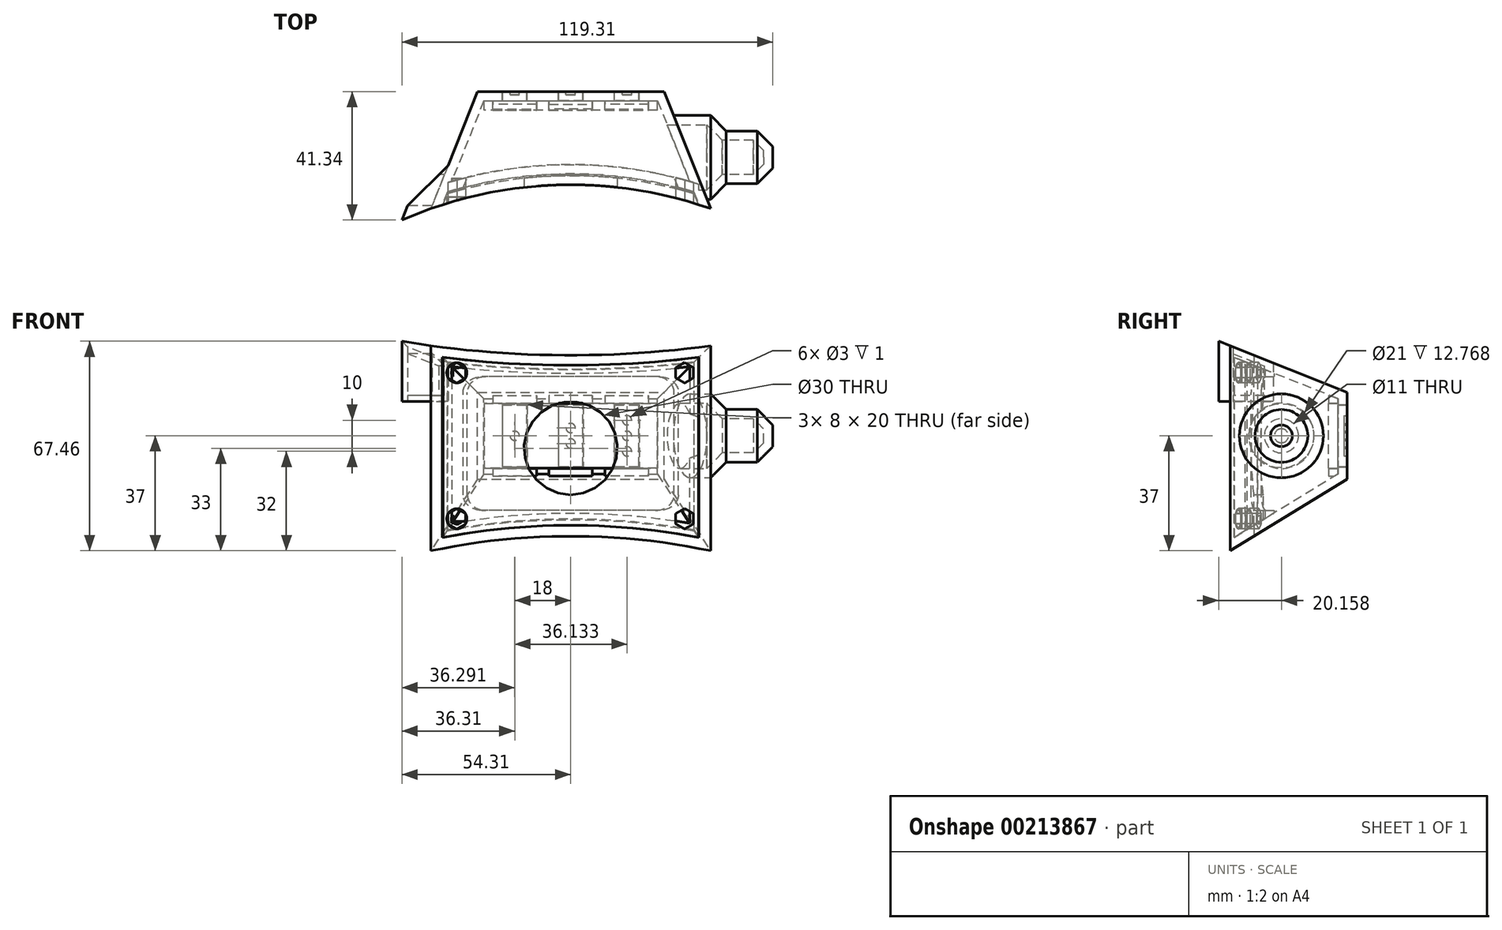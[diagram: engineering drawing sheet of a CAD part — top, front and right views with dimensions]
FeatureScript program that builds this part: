
annotation { "Feature Type Name" : "Feature", "Feature Type Description" : "" }
export const myFeature = defineFeature(function(context is Context, id is Id, definition is map)
    precondition{}
    {
        {
            var Q0;
            Q0=qCreatedBy(makeId("Top.planeOp"),FACE);
            var sketch = newSketch(context, id + "F0", { "sketchPlane" : qUnion([Q0])});
            skLineSegment(sketch, "E0", {"start": v(-72.5, 0) * mm, "end": v(72.5, 0) * mm});
            skPoint(sketch, "E1", {"position": v(0, 0) * mm});
            skLineSegment(sketch, "E2", {"start": v(0, 0) * mm, "end": v(0, 21) * mm, "construction": true});
            skArc(sketch, "E3", {"start": v(72.5, 0) * mm, "mid": v(0, 21) * mm, "end": v(-72.5, 0) * mm});
            skLineSegment(sketch, "E4", {"start": v(-45, 0) * mm, "end": v(45, 0) * mm, "construction": true});
            skLineSegment(sketch, "E5", {"start": v(-45, 0) * mm, "end": v(-45, 13.32) * mm, "construction": true});
            skLineSegment(sketch, "E6", {"start": v(45, 0) * mm, "end": v(45, 13.32) * mm, "construction": true});
            skLineSegment(sketch, "E7", {"start": v(45, 13.32) * mm, "end": v(-45, 13.32) * mm});
            skPoint(sketch, "E8", {"position": v(-41.1, 13.32) * mm});
            skPoint(sketch, "E9.MirrorP", {"position": v(41.1, 13.32) * mm});
            skLineSegment(sketch, "E10.MirrorCS", {"start": v(-45, 13.32) * mm, "end": v(45, 13.32) * mm, "construction": true});
            skLineSegment(sketch, "E11", {"start": v(-41.1, 13.32) * mm, "end": v(-41.1, 14.62) * mm, "construction": true});
            skLineSegment(sketch, "E12.MirrorCS", {"start": v(41.1, 13.32) * mm, "end": v(41.1, 14.62) * mm, "construction": true});
            skLineSegment(sketch, "E13", {"start": v(-41.1, 14.62) * mm, "end": v(41.1, 14.62) * mm});
            skPoint(sketch, "E14", {"position": v(0, 24) * mm});
            skLineSegment(sketch, "E15", {"start": v(-41.1, 14.62) * mm, "end": v(-39.65, 18.2) * mm});
            skLineSegment(sketch, "E16.MirrorCS", {"start": v(41.1, 14.62) * mm, "end": v(39.65, 18.2) * mm});
            skArc(sketch, "E17", {"start": v(39.65, 18.2) * mm, "mid": v(0, 24) * mm, "end": v(-39.65, 18.2) * mm});
            skPoint(sketch, "E18", {"position": v(-41.15, 18.2) * mm});
            skPoint(sketch, "E19", {"position": v(0, 24.5) * mm});
            skPoint(sketch, "E20.MirrorP", {"position": v(41.15, 18.2) * mm});
            skArc(sketch, "E21", {"start": v(41.15, 18.2) * mm, "mid": v(0, 24.5) * mm, "end": v(-41.15, 18.2) * mm});
            skPoint(sketch, "E22", {"position": v(0, 27.5) * mm});
            skPoint(sketch, "E23", {"position": v(-41.15, 21.2) * mm});
            skPoint(sketch, "E24.MirrorP", {"position": v(41.15, 21.2) * mm});
            skArc(sketch, "E25", {"start": v(41.15, 21.2) * mm, "mid": v(0, 27.5) * mm, "end": v(-41.15, 21.2) * mm});
            skLineSegment(sketch, "E26", {"start": v(41.15, 21.2) * mm, "end": v(41.15, 18.2) * mm});
            skLineSegment(sketch, "E27", {"start": v(-41.15, 21.2) * mm, "end": v(-41.15, 18.2) * mm});
            skSolve(sketch);
        }
        {
            var Q0;
            Q0=qCreatedBy(makeId("Front.planeOp"),FACE);
            var sketch = newSketch(context, id + "F1", { "sketchPlane" : qUnion([Q0])});
            skLineSegment(sketch, "E28.bottom", {"start": v(-45, 33) * mm, "end": v(45, 33) * mm});
            skLineSegment(sketch, "E28.top", {"start": v(-45, -33) * mm, "end": v(45, -33) * mm});
            skLineSegment(sketch, "E28.left", {"start": v(-45, 33) * mm, "end": v(-45, -33) * mm});
            skLineSegment(sketch, "E28.right", {"start": v(45, 33) * mm, "end": v(45, -33) * mm});
            skPoint(sketch, "E28.middle", {"position": v(0, 0) * mm});
            skLineSegment(sketch, "E29.bottom", {"start": v(75, 33) * mm, "end": v(-75, 33) * mm, "construction": true});
            skLineSegment(sketch, "E29.top", {"start": v(75, -7) * mm, "end": v(-75, -7) * mm, "construction": true});
            skLineSegment(sketch, "E29.left", {"start": v(75, 33) * mm, "end": v(75, -7) * mm, "construction": true});
            skLineSegment(sketch, "E29.right", {"start": v(-75, 33) * mm, "end": v(-75, -7) * mm, "construction": true});
            skPoint(sketch, "E30.positionSnap0", {"position": v(0, -7) * mm});
            skSolve(sketch);
        }
        {
            var Q0;
            Q0=makeQuery(id+"F1.imprint","IMPRINT",FACE,{"disambiguationData":[TD([[makeQuery(id+"F1.imprint","IMPRINT",EDGE,{"derivedFrom":sQuery(id+"F1.wireOp",EDGE,"E28.bottom")}),-1.0]])]});
            extrude(context, id + "F2", {"entities" : qUnion([Q0]), "oppositeDirection" : true, "depth" : 51 * mm});
        }
        {
            var Q0;
            Q0=makeQuery(id+"F0.imprint","IMPRINT",FACE,{"disambiguationData":[TD([[makeQuery(id+"F0.imprint","IMPRINT",EDGE,{"derivedFrom":sQuery(id+"F0.wireOp",EDGE,"E0")}),1.0]])]});
            var Q1;
            {var subQ0=sQuery(id+"F0.wireOp",EDGE,"E7");Q1=makeQuery(id+"F0.imprint","IMPRINT",FACE,{"disambiguationData":[TD([[makeQuery(id+"F0.imprint","IMPRINT",EDGE,{"derivedFrom":subQ0}),-1.0]])]});}
            var Q2;
            {var subQ0=sQuery(id+"F0.wireOp",EDGE,"E13");Q2=makeQuery(id+"F0.imprint","IMPRINT",FACE,{"disambiguationData":[TD([[makeQuery(id+"F0.imprint","IMPRINT",EDGE,{"derivedFrom":subQ0}),1.0]])]});}
            var Q3;
            Q3 = qConstructionFilter(qBodyType(qCreatedBy(id + "F0" ,EDGE), BodyType.WIRE), ConstructionObject.NO);
            var Q4;
            Q4=makeQuery(id+"F2.opExtrude","SWEPT_FACE",FACE,{"disambiguationData":[OSD([sQuery(id+"F1.wireOp",EDGE,"E28.bottom")])]});
            var Q5;
            Q5=makeQuery(id+"F2.opExtrude","SWEPT_FACE",FACE,{"disambiguationData":[OSD([sQuery(id+"F1.wireOp",EDGE,"E28.top")])]});
            extrude(context, id + "F3", {"entities" : qUnion([Q0, Q1, Q2]), "operationType" : NewBodyOperationType.REMOVE, "surfaceEntities" : qUnion([Q3]), "endBound" : BoundingType.UP_TO_SURFACE, "endBoundEntityFace" : qUnion([Q4]), "depth" : 25 * mm, "hasSecondDirection" : true, "secondDirectionBound" : SecondDirectionBoundingType.UP_TO_SURFACE, "secondDirectionOppositeDirection" : true, "secondDirectionBoundEntityFace" : qUnion([Q5]), "secondDirectionDepth" : 25 * mm});
        }
        {
            var Q0;
            Q0=makeQuery(id+"F2.opExtrude","SWEPT_FACE",FACE,{"disambiguationData":[OSD([sQuery(id+"F1.wireOp",EDGE,"E28.bottom")])]});
            var sketch = newSketch(context, id + "F4", { "sketchPlane" : qUnion([Q0])});
            skLineSegment(sketch, "E31", {"start": v(-30, 51) * mm, "end": v(30, 51) * mm, "construction": true});
            skPoint(sketch, "E32", {"position": v(0, 51) * mm});
            skPoint(sketch, "E33", {"position": v(-45, 13.32) * mm});
            skPoint(sketch, "E34.MirrorP", {"position": v(45, 13.32) * mm});
            skLineSegment(sketch, "E35", {"start": v(-30, 51) * mm, "end": v(-45, 13.32) * mm});
            skLineSegment(sketch, "E36", {"start": v(30, 51) * mm, "end": v(45, 13.32) * mm});
            skSolve(sketch);
        }
        {
            var Q0;
            {var subQ0=sQuery(id+"F4.wireOp",EDGE,"E35");Q0=makeQuery(id+"F4.imprint","IMPRINT",FACE,{"disambiguationData":[TD([[makeQuery(id+"F4.imprint","IMPRINT",EDGE,{"derivedFrom":subQ0}),-1.0]])]});}
            var Q1;
            {var subQ0=sQuery(id+"F4.wireOp",EDGE,"E36");Q1=makeQuery(id+"F4.imprint","IMPRINT",FACE,{"disambiguationData":[TD([[makeQuery(id+"F4.imprint","IMPRINT",EDGE,{"derivedFrom":subQ0}),1.0]])]});}
            var Q2;
            Q2=makeQuery(id+"F2.opExtrude","SWEPT_FACE",FACE,{"disambiguationData":[OSD([sQuery(id+"F1.wireOp",EDGE,"E28.top")])]});
            extrude(context, id + "F5", {"entities" : qUnion([Q0, Q1]), "operationType" : NewBodyOperationType.REMOVE, "endBound" : BoundingType.UP_TO_SURFACE, "oppositeDirection" : true, "endBoundEntityFace" : qUnion([Q2]), "depth" : 25 * mm});
        }
        {
            var Q0;
            Q0=qCreatedBy(makeId("Top.planeOp"),FACE);
            cPlane(context, id + "F6", {"entities" : qUnion([Q0]), "cplaneType" : CPlaneType.OFFSET, "offset" : 15 * mm, "width" : 150 * mm, "height" : 150 * mm});
        }
        {
            var Q0;
            Q0=qCreatedBy(makeId("Right.planeOp"),FACE);
            var sketch = newSketch(context, id + "F7", { "sketchPlane" : qUnion([Q0])});
            skLineSegment(sketch, "E37", {"start": v(13.32, -33) * mm, "end": v(51, -10) * mm});
            skLineSegment(sketch, "E38", {"start": v(13.32, 33) * mm, "end": v(51, 18) * mm});
            skLineSegment(sketch, "E39", {"start": v(51, 18) * mm, "end": v(51, 33) * mm});
            skLineSegment(sketch, "E40", {"start": v(51, 33) * mm, "end": v(13.32, 33) * mm});
            skLineSegment(sketch, "E41", {"start": v(13.32, -33) * mm, "end": v(51, -33) * mm});
            skLineSegment(sketch, "E42", {"start": v(51, -33) * mm, "end": v(51, -10) * mm});
            skSolve(sketch);
        }
        {
            var Q0;
            Q0=makeQuery(id+"F7.imprint","IMPRINT",FACE,{"disambiguationData":[TD([[makeQuery(id+"F7.imprint","IMPRINT",EDGE,{"derivedFrom":sQuery(id+"F7.wireOp",EDGE,"E38")}),1.0]])]});
            var Q1;
            Q1=makeQuery(id+"F7.imprint","IMPRINT",FACE,{"disambiguationData":[TD([[makeQuery(id+"F7.imprint","IMPRINT",EDGE,{"derivedFrom":sQuery(id+"F7.wireOp",EDGE,"E37")}),-1.0]])]});
            extrude(context, id + "F8", {"entities" : qUnion([Q0, Q1]), "operationType" : NewBodyOperationType.REMOVE, "oppositeDirection" : true, "depth" : 50 * mm, "hasSecondDirection" : true, "secondDirectionOppositeDirection" : false, "secondDirectionDepth" : 50 * mm});
        }
        {
            var Q0;
            Q0=makeQuery(id+"F2.opExtrude","CAP_FACE",FACE,{"disambiguationData":[OSD([sQuery(id+"F1.wireOp",EDGE,"E28.bottom"),sQuery(id+"F1.wireOp",EDGE,"E28.top"),sQuery(id+"F1.wireOp",EDGE,"E28.left"),sQuery(id+"F1.wireOp",EDGE,"E28.right")])],"isStart":false});
            var sketch = newSketch(context, id + "F9", { "sketchPlane" : qUnion([Q0])});
            skLineSegment(sketch, "E43.bottom", {"start": v(-22, 14) * mm, "end": v(-14, 14) * mm});
            skLineSegment(sketch, "E43.top", {"start": v(-22, -6) * mm, "end": v(-14, -6) * mm});
            skLineSegment(sketch, "E43.left", {"start": v(-22, 14) * mm, "end": v(-22, -6) * mm});
            skLineSegment(sketch, "E43.right", {"start": v(-14, 14) * mm, "end": v(-14, -6) * mm});
            skLineSegment(sketch, "E44.bottom", {"start": v(-4, 14) * mm, "end": v(0, 14) * mm});
            skLineSegment(sketch, "E44.top", {"start": v(-4, -6) * mm, "end": v(0, -6) * mm});
            skLineSegment(sketch, "E44.left", {"start": v(-4, 14) * mm, "end": v(-4, -6) * mm});
            skLineSegment(sketch, "E44.right", {"start": v(0, 14) * mm, "end": v(0, -6) * mm});
            skLineSegment(sketch, "E45.MirrorCS", {"start": v(22, 14) * mm, "end": v(14, 14) * mm});
            skLineSegment(sketch, "E46.MirrorCS", {"start": v(22, 14) * mm, "end": v(22, -6) * mm});
            skLineSegment(sketch, "E47.MirrorCS", {"start": v(22, -6) * mm, "end": v(14, -6) * mm});
            skLineSegment(sketch, "E48.MirrorCS", {"start": v(14, 14) * mm, "end": v(14, -6) * mm});
            skLineSegment(sketch, "E49.MirrorCS", {"start": v(4, -6) * mm, "end": v(0, -6) * mm});
            skLineSegment(sketch, "E50.MirrorCS", {"start": v(4, 14) * mm, "end": v(4, -6) * mm});
            skLineSegment(sketch, "E51.MirrorCS", {"start": v(4, 14) * mm, "end": v(0, 14) * mm});
            skLineSegment(sketch, "E52", {"start": v(0, 18) * mm, "end": v(0, -10) * mm, "construction": true});
            skPoint(sketch, "E53", {"position": v(0, 4) * mm});
            skPoint(sketch, "E54", {"position": v(-4, 4) * mm});
            skSolve(sketch);
        }
        {
            var Q0;
            Q0=makeQuery(id+"F9.imprint","IMPRINT",FACE,{"disambiguationData":[TD([[makeQuery(id+"F9.imprint","IMPRINT",EDGE,{"derivedFrom":sQuery(id+"F9.wireOp",EDGE,"E43.bottom")}),-1.0]])]});
            var Q1;
            Q1=makeQuery(id+"F9.imprint","IMPRINT",FACE,{"disambiguationData":[TD([[makeQuery(id+"F9.imprint","IMPRINT",EDGE,{"derivedFrom":sQuery(id+"F9.wireOp",EDGE,"E44.bottom")}),-1.0]])]});
            var Q2;
            Q2=makeQuery(id+"F9.imprint","IMPRINT",FACE,{"disambiguationData":[TD([[makeQuery(id+"F9.imprint","IMPRINT",EDGE,{"derivedFrom":sQuery(id+"F9.wireOp",EDGE,"E44.right")}),1.0]])]});
            var Q3;
            Q3=makeQuery(id+"F9.imprint","IMPRINT",FACE,{"disambiguationData":[TD([[makeQuery(id+"F9.imprint","IMPRINT",EDGE,{"derivedFrom":sQuery(id+"F9.wireOp",EDGE,"E45.MirrorCS")}),1.0]])]});
            extrude(context, id + "F10", {"entities" : qUnion([Q0, Q1, Q2, Q3]), "operationType" : NewBodyOperationType.REMOVE, "oppositeDirection" : true, "depth" : 3 * mm});
        }
        {
            var Q0;
            Q0=qCreatedBy(id+"F6.planeOp",FACE);
            var sketch = newSketch(context, id + "F11", { "sketchPlane" : qUnion([Q0])});
            skLineSegment(sketch, "E55", {"start": v(-39.45, 27.25) * mm, "end": v(-45, 13.32) * mm});
            skLineSegment(sketch, "E56", {"start": v(-45, 13.32) * mm, "end": v(-54.3, 9.66) * mm});
            skLineSegment(sketch, "E57", {"start": v(-54.3, 9.66) * mm, "end": v(-52.46, 14.3) * mm});
            skLineSegment(sketch, "E58", {"start": v(-52.46, 14.3) * mm, "end": v(-39.45, 27.25) * mm});
            skSolve(sketch);
        }
        {
            var Q0;
            Q0=makeQuery(id+"F11.imprint","IMPRINT",FACE,{"disambiguationData":[TD([[makeQuery(id+"F11.imprint","IMPRINT",EDGE,{"derivedFrom":sQuery(id+"F11.wireOp",EDGE,"E55")}),-1.0]])]});
            var Q1;
            Q1=makeQuery(id+"F8.boolean.opBoolean","COPY",FACE,{"derivedFrom":makeQuery(id+"F8.opExtrude","SWEPT_FACE",FACE,{"disambiguationData":[OSD([sQuery(id+"F7.wireOp",EDGE,"E38")])]})});
            extrude(context, id + "F12", {"entities" : qUnion([Q0]), "operationType" : NewBodyOperationType.ADD, "endBound" : BoundingType.UP_TO_SURFACE, "endBoundEntityFace" : qUnion([Q1]), "depth" : 25 * mm});
        }
        {
            var Q0;
            Q0=qCreatedBy(makeId("Right.planeOp"),FACE);
            cPlane(context, id + "F13", {"entities" : qUnion([Q0]), "cplaneType" : CPlaneType.OFFSET, "offset" : 60 * mm, "oppositeDirection" : true, "width" : 150 * mm, "height" : 150 * mm});
        }
        {
            var Q0;
            Q0=qCreatedBy(id+"F13.planeOp",FACE);
            var sketch = newSketch(context, id + "F14", { "sketchPlane" : qUnion([Q0])});
            skLineSegment(sketch, "E59", {"start": v(14.3, 30.46) * mm, "end": v(24.3, 26.48) * mm});
            skLineSegment(sketch, "E60", {"start": v(24.3, 26.48) * mm, "end": v(24.3, 17) * mm});
            skLineSegment(sketch, "E61", {"start": v(24.3, 17) * mm, "end": v(14.3, 17) * mm});
            skLineSegment(sketch, "E62", {"start": v(14.3, 17) * mm, "end": v(14.3, 30.46) * mm});
            skSolve(sketch);
        }
        {
            var Q0;
            Q0=makeQuery(id+"F14.imprint","IMPRINT",FACE,{"disambiguationData":[TD([[makeQuery(id+"F14.imprint","IMPRINT",EDGE,{"derivedFrom":sQuery(id+"F14.wireOp",EDGE,"E59")}),-1.0]])]});
            var Q1;
            Q1=makeQuery(id+"F5.boolean.opBoolean","COPY",FACE,{"derivedFrom":makeQuery(id+"F5.opExtrude","SWEPT_FACE",FACE,{"disambiguationData":[OSD([sQuery(id+"F4.wireOp",EDGE,"E35")])]})});
            extrude(context, id + "F15", {"entities" : qUnion([Q0]), "operationType" : NewBodyOperationType.REMOVE, "endBound" : BoundingType.UP_TO_SURFACE, "endBoundEntityFace" : qUnion([Q1]), "depth" : 25 * mm});
        }
        {
            var Q0;
            Q0=qCreatedBy(makeId("Right.planeOp"),FACE);
            cPlane(context, id + "F16", {"entities" : qUnion([Q0]), "cplaneType" : CPlaneType.OFFSET, "offset" : 50 * mm, "width" : 150 * mm, "height" : 150 * mm});
        }
        {
            var Q0;
            Q0=qCreatedBy(id+"F16.planeOp",FACE);
            var sketch = newSketch(context, id + "F17", { "sketchPlane" : qUnion([Q0])});
            skPoint(sketch, "E63", {"position": v(51, 4) * mm});
            skLineSegment(sketch, "E64", {"start": v(51, 4) * mm, "end": v(13.32, 4) * mm, "construction": true});
            skCircle(sketch, "E65", {"center": v(29.82, 4) * mm, "radius": 13.5 * mm});
            skCircle(sketch, "E66", {"center": v(29.82, 4) * mm, "radius": 8.5 * mm});
            skPoint(sketch, "E67", {"position": v(16.32, 4) * mm});
            skSolve(sketch);
        }
        {
            var Q0;
            Q0=makeQuery(id+"F17.imprint","IMPRINT",FACE,{"disambiguationData":[TD([[makeQuery(id+"F17.imprint","IMPRINT",EDGE,{"derivedFrom":sQuery(id+"F17.wireOp",EDGE,"E66")}),1.0]])]});
            var Q1;
            Q1=makeQuery(id+"F17.imprint","IMPRINT",FACE,{"disambiguationData":[TD([[makeQuery(id+"F17.imprint","IMPRINT",EDGE,{"derivedFrom":sQuery(id+"F17.wireOp",EDGE,"E65")}),1.0]])]});
            var Q2;
            Q2=makeQuery(id+"F5.boolean.opBoolean","COPY",FACE,{"derivedFrom":makeQuery(id+"F5.opExtrude","SWEPT_FACE",FACE,{"disambiguationData":[OSD([sQuery(id+"F4.wireOp",EDGE,"E36")])]})});
            extrude(context, id + "F18", {"entities" : qUnion([Q0, Q1]), "operationType" : NewBodyOperationType.ADD, "endBound" : BoundingType.UP_TO_SURFACE, "oppositeDirection" : true, "endBoundEntityFace" : qUnion([Q2]), "depth" : 25 * mm});
        }
        {
            var Q0;
            Q0=makeQuery(id+"F17.imprint","IMPRINT",FACE,{"disambiguationData":[TD([[makeQuery(id+"F17.imprint","IMPRINT",EDGE,{"derivedFrom":sQuery(id+"F17.wireOp",EDGE,"E66")}),1.0]])]});
            extrude(context, id + "F19", {"entities" : qUnion([Q0]), "operationType" : NewBodyOperationType.ADD, "depth" : 15 * mm});
        }
        {
            var Q0;
            Q0=makeQuery(id+"F18.opExtrude","CAP_EDGE",EDGE,{"disambiguationData":[OSD([sQuery(id+"F17.wireOp",EDGE,"E65")])],"isStart":true});
            var Q1;
            Q1=makeQuery(id+"F19.opExtrude","CAP_EDGE",EDGE,{"disambiguationData":[OSD([sQuery(id+"F17.wireOp",EDGE,"E66")])],"isStart":false});
            chamfer(context, id + "F20", {"entities" : qUnion([Q0, Q1]), "width" : 5 * mm, "tangentPropagation" : true});
        }
        {
            var Q0;
            Q0=makeQuery(id+"F3.boolean.opBoolean","COPY",FACE,{"derivedFrom":makeQuery(id+"F3.opExtrude","SWEPT_FACE",FACE,{"disambiguationData":[OSD([sQuery(id+"F0.wireOp",EDGE,"E3")])]})});
            var Q1;
            Q1=makeQuery(id+"F2.opExtrude","SWEPT_BODY",BODY,{"disambiguationData":[OSD([sQuery(id+"F1.wireOp",EDGE,"E28.bottom"),sQuery(id+"F1.wireOp",EDGE,"E28.top"),sQuery(id+"F1.wireOp",EDGE,"E28.left"),sQuery(id+"F1.wireOp",EDGE,"E28.right")])]});
            shell(context, id + "F21", {"entities" : qUnion([Q0]), "parts" : qUnion([Q1]), "thickness" : 3 * mm});
        }
        {
            var Q0;
            Q0=makeQuery(id+"F21.opShell","OFFSET_FACE",FACE,{"disambiguationData":[OSD([sQuery(id+"F9.wireOp",EDGE,"E44.bottom"),sQuery(id+"F9.wireOp",EDGE,"E44.top"),sQuery(id+"F9.wireOp",EDGE,"E44.left"),sQuery(id+"F9.wireOp",EDGE,"E49.MirrorCS"),sQuery(id+"F9.wireOp",EDGE,"E50.MirrorCS"),sQuery(id+"F9.wireOp",EDGE,"E51.MirrorCS")])]});
            var sketch = newSketch(context, id + "F22", { "sketchPlane" : qUnion([Q0])});
            skLineSegment(sketch, "E68.bottom", {"start": v(-27.5, -6.5) * mm, "end": v(27.5, -6.5) * mm});
            skLineSegment(sketch, "E68.top", {"start": v(-27.5, 14.5) * mm, "end": v(27.5, 14.5) * mm});
            skLineSegment(sketch, "E68.left", {"start": v(-27.5, -6.5) * mm, "end": v(-27.5, 14.5) * mm});
            skLineSegment(sketch, "E68.right", {"start": v(27.5, -6.5) * mm, "end": v(27.5, 14.5) * mm});
            skPoint(sketch, "E69", {"position": v(0, -6.5) * mm});
            skSolve(sketch);
        }
        {
            var Q0;
            {var subQ0=sQuery(id+"F22.wireOp",EDGE,"E68.left");Q0=makeQuery(id+"F22.imprint","IMPRINT",FACE,{"disambiguationData":[TD([[makeQuery(id+"F22.imprint","IMPRINT",EDGE,{"derivedFrom":subQ0}),-1.0]])]});}
            var Q1;
            {var subQ0=sQuery(id+"F22.wireOp",EDGE,"E68.bottom");var subQ1=sQuery(id+"F9.wireOp",EDGE,"E50.MirrorCS");var subQ2=makeQuery(id+"F21.opShell","OFFSET_EDGE",EDGE,{"disambiguationData":[OSD([subQ1]),TDD([makeQuery(id+"F10.boolean.opBoolean","COPY",EDGE,{"derivedFrom":makeQuery(id+"F10.opExtrude","CAP_EDGE",EDGE,{"disambiguationData":[OSD([subQ1])],"isStart":false})})])]});var subQ3=makeQuery(id+"F22.imprint","INTERSECT",VERTEX,{"derivedFrom":[subQ2,subQ0]});Q1=makeQuery(id+"F22.imprint","IMPRINT",FACE,{"disambiguationData":[TD([[makeQuery(id+"F22.imprint","IMPRINT",EDGE,{"disambiguationData":[TD([[subQ3,-1.0]])],"derivedFrom":subQ0}),1.0]])]});}
            var Q2;
            {var subQ0=sQuery(id+"F22.wireOp",EDGE,"E68.right");Q2=makeQuery(id+"F22.imprint","IMPRINT",FACE,{"disambiguationData":[TD([[makeQuery(id+"F22.imprint","IMPRINT",EDGE,{"derivedFrom":subQ0}),1.0]])]});}
            extrude(context, id + "F23", {"entities" : qUnion([Q0, Q1, Q2]), "operationType" : NewBodyOperationType.REMOVE, "oppositeDirection" : true, "depth" : 3 * mm});
        }
        {
            var Q0;
            {var subQ0=sQuery(id+"F0.wireOp",EDGE,"E15");Q0=makeQuery(id+"F0.imprint","IMPRINT",FACE,{"disambiguationData":[TD([[makeQuery(id+"F0.imprint","IMPRINT",EDGE,{"derivedFrom":subQ0}),-1.0]])]});}
            var Q1;
            Q1=makeQuery(id+"F21.opShell","OFFSET_FACE",FACE,{"disambiguationData":[OSD([sQuery(id+"F7.wireOp",EDGE,"E38")])]});
            var Q2;
            Q2=makeQuery(id+"F21.opShell","OFFSET_FACE",FACE,{"disambiguationData":[OSD([sQuery(id+"F7.wireOp",EDGE,"E37")])]});
            extrude(context, id + "F24", {"entities" : qUnion([Q0]), "endBound" : BoundingType.UP_TO_NEXT, "oppositeDirection" : true, "endBoundEntityFace" : qUnion([Q1]), "depth" : 19 * mm, "hasSecondDirection" : true, "secondDirectionBound" : SecondDirectionBoundingType.UP_TO_NEXT, "secondDirectionOppositeDirection" : false, "secondDirectionBoundEntityFace" : qUnion([Q2]), "secondDirectionDepth" : 20 * mm});
        }
        {
            var Q0;
            Q0=makeQuery(id+"F0.imprint","IMPRINT",FACE,{"disambiguationData":[TD([[makeQuery(id+"F0.imprint","IMPRINT",EDGE,{"derivedFrom":sQuery(id+"F0.wireOp",EDGE,"E21")}),-1.0]])]});
            var Q1;
            Q1=makeQuery(id+"F12.boolean.opBoolean","MERGE",FACE,{"derivedFrom":[makeQuery(id+"F8.boolean.opBoolean","COPY",FACE,{"derivedFrom":makeQuery(id+"F8.opExtrude","SWEPT_FACE",FACE,{"disambiguationData":[OSD([sQuery(id+"F7.wireOp",EDGE,"E38")])]})}),makeQuery(id+"F12.opExtrude","CAP_FACE",FACE,{"disambiguationData":[OSD([sQuery(id+"F11.wireOp",EDGE,"E55"),sQuery(id+"F11.wireOp",EDGE,"E56"),sQuery(id+"F11.wireOp",EDGE,"E57"),sQuery(id+"F11.wireOp",EDGE,"E58")])],"isStart":false})]});
            extrude(context, id + "F25", {"entities" : qUnion([Q0]), "operationType" : NewBodyOperationType.ADD, "endBound" : BoundingType.UP_TO_SURFACE, "endBoundEntityFace" : qUnion([Q1]), "depth" : 25 * mm});
        }
        {
            var Q0;
            Q0=makeQuery(id+"F0.imprint","IMPRINT",FACE,{"disambiguationData":[TD([[makeQuery(id+"F0.imprint","IMPRINT",EDGE,{"derivedFrom":sQuery(id+"F0.wireOp",EDGE,"E21")}),-1.0]])]});
            var Q1;
            Q1=makeQuery(id+"F8.boolean.opBoolean","COPY",FACE,{"derivedFrom":makeQuery(id+"F8.opExtrude","SWEPT_FACE",FACE,{"disambiguationData":[OSD([sQuery(id+"F7.wireOp",EDGE,"E37")])]})});
            extrude(context, id + "F26", {"entities" : qUnion([Q0]), "operationType" : NewBodyOperationType.ADD, "endBound" : BoundingType.UP_TO_SURFACE, "oppositeDirection" : true, "endBoundEntityFace" : qUnion([Q1]), "depth" : 25 * mm});
        }
        {
            var Q0;
            Q0=makeQuery(id+"F0.imprint","IMPRINT",FACE,{"disambiguationData":[TD([[makeQuery(id+"F0.imprint","IMPRINT",EDGE,{"derivedFrom":sQuery(id+"F0.wireOp",EDGE,"E21")}),-1.0]])]});
            var sketch = newSketch(context, id + "F27", { "sketchPlane" : qUnion([Q0])});
            skLineSegment(sketch, "E70", {"start": v(-34.65, 19.97) * mm, "end": v(-33.2, 23.54) * mm});
            skPoint(sketch, "E71", {"position": v(0, 27.6) * mm});
            skPoint(sketch, "E72", {"position": v(0, 24.4) * mm});
            skLineSegment(sketch, "E73.MirrorCS", {"start": v(34.65, 19.97) * mm, "end": v(33.2, 23.54) * mm});
            skArc(sketch, "E74", {"start": v(33.2, 23.54) * mm, "mid": v(0, 27.6) * mm, "end": v(-33.2, 23.54) * mm});
            skArc(sketch, "E75", {"start": v(34.65, 19.97) * mm, "mid": v(0, 24.4) * mm, "end": v(-34.65, 19.97) * mm});
            skSolve(sketch);
        }
        {
            var Q0;
            {var subQ0=sQuery(id+"F27.wireOp",EDGE,"E70");var subQ1=makeQuery(id+"F0.imprint","IMPRINT",EDGE,{"derivedFrom":sQuery(id+"F0.wireOp",EDGE,"E21")});var subQ2=makeQuery(id+"F27.imprint","INTERSECT",VERTEX,{"derivedFrom":[subQ1,subQ0]});Q0=makeQuery(id+"F27.imprint","IMPRINT",FACE,{"disambiguationData":[TD([[makeQuery(id+"F27.imprint","IMPRINT",EDGE,{"disambiguationData":[TD([[subQ2,-1.0]])],"derivedFrom":subQ0}),-1.0]])]});}
            extrude(context, id + "F28", {"entities" : qUnion([Q0]), "operationType" : NewBodyOperationType.REMOVE, "oppositeDirection" : true, "depth" : 20 * mm, "hasSecondDirection" : true, "secondDirectionOppositeDirection" : false, "secondDirectionDepth" : 23 * mm});
        }
        {
            var Q0;
            Q0=qCreatedBy(makeId("Front.planeOp"),FACE);
            var sketch = newSketch(context, id + "F29", { "sketchPlane" : qUnion([Q0])});
            skLineSegment(sketch, "E76", {"start": v(-42.3, 23) * mm, "end": v(42.3, 23) * mm, "construction": true});
            skLineSegment(sketch, "E77", {"start": v(-34.6, 30.27) * mm, "end": v(-34.6, 17.28) * mm, "construction": true});
            skCircle(sketch, "E78", {"center": v(-36.64, 24.3) * mm, "radius": 1.75 * mm});
            skCircle(sketch, "E79", {"center": v(-36.64, 24.3) * mm, "radius": 3 * mm});
            skPoint(sketch, "E80", {"position": v(-39.64, 24.3) * mm});
            skPoint(sketch, "E81", {"position": v(-36.64, 27.3) * mm});
            skCircle(sketch, "E82.MirrorC", {"center": v(36.64, 24.3) * mm, "radius": 1.75 * mm});
            skLineSegment(sketch, "E83", {"start": v(-42.64, -20) * mm, "end": v(45.56, -20) * mm, "construction": true});
            skLineSegment(sketch, "E84", {"start": v(-34.6, -14.38) * mm, "end": v(-34.6, -27.87) * mm, "construction": true});
            skCircle(sketch, "E85", {"center": v(-36.64, -22.69) * mm, "radius": 1.75 * mm});
            skCircle(sketch, "E86", {"center": v(-36.64, -22.69) * mm, "radius": 3 * mm});
            skPoint(sketch, "E87", {"position": v(-39.64, -22.69) * mm});
            skPoint(sketch, "E88", {"position": v(-36.64, -25.69) * mm});
            skCircle(sketch, "E89.MirrorC", {"center": v(36.64, -22.69) * mm, "radius": 1.75 * mm});
            skCircle(sketch, "E90", {"center": v(0, 0) * mm, "radius": 15 * mm});
            skSolve(sketch);
        }
        {
            var Q0;
            Q0=makeQuery(id+"F28.boolean.opBoolean","COPY",EDGE,{"derivedFrom":makeQuery(id+"F28.opExtrude","CAP_EDGE",EDGE,{"disambiguationData":[OSD([sQuery(id+"F27.wireOp",EDGE,"E70")])],"isStart":true})});
            var Q1;
            Q1=makeQuery(id+"F28.boolean.opBoolean","COPY",EDGE,{"derivedFrom":makeQuery(id+"F28.opExtrude","CAP_EDGE",EDGE,{"disambiguationData":[OSD([sQuery(id+"F27.wireOp",EDGE,"E73.MirrorCS")])],"isStart":true})});
            var Q2;
            Q2=makeQuery(id+"F28.boolean.opBoolean","COPY",EDGE,{"derivedFrom":makeQuery(id+"F28.opExtrude","CAP_EDGE",EDGE,{"disambiguationData":[OSD([sQuery(id+"F27.wireOp",EDGE,"E73.MirrorCS")])],"isStart":false})});
            var Q3;
            Q3=makeQuery(id+"F28.boolean.opBoolean","COPY",EDGE,{"derivedFrom":makeQuery(id+"F28.opExtrude","CAP_EDGE",EDGE,{"disambiguationData":[OSD([sQuery(id+"F27.wireOp",EDGE,"E70")])],"isStart":false})});
            fillet(context, id + "F30", {"entities" : qUnion([Q0, Q1, Q2, Q3]), "radius" : 5 * mm, "tangentPropagation" : true, "allowEdgeOverflow" : false});
        }
        {
            var Q0;
            Q0=makeQuery(id+"F29.imprint","IMPRINT",FACE,{"disambiguationData":[TD([[makeQuery(id+"F29.imprint","IMPRINT",EDGE,{"derivedFrom":sQuery(id+"F29.wireOp",EDGE,"E78")}),1.0]])]});
            var Q1;
            Q1=makeQuery(id+"F29.imprint","IMPRINT",FACE,{"disambiguationData":[TD([[makeQuery(id+"F29.imprint","IMPRINT",EDGE,{"derivedFrom":sQuery(id+"F29.wireOp",EDGE,"E82.MirrorC")}),-1.0]])]});
            var Q2;
            Q2=makeQuery(id+"F29.imprint","IMPRINT",FACE,{"disambiguationData":[TD([[makeQuery(id+"F29.imprint","IMPRINT",EDGE,{"derivedFrom":sQuery(id+"F29.wireOp",EDGE,"E89.MirrorC")}),-1.0]])]});
            var Q3;
            Q3=makeQuery(id+"F29.imprint","IMPRINT",FACE,{"disambiguationData":[TD([[makeQuery(id+"F29.imprint","IMPRINT",EDGE,{"derivedFrom":sQuery(id+"F29.wireOp",EDGE,"E85")}),1.0]])]});
            extrude(context, id + "F31", {"entities" : qUnion([Q0, Q1, Q2, Q3]), "operationType" : NewBodyOperationType.REMOVE, "oppositeDirection" : true, "depth" : 23 * mm});
        }
        {
            var Q0;
            Q0=makeQuery(id+"F29.imprint","IMPRINT",FACE,{"disambiguationData":[TD([[makeQuery(id+"F29.imprint","IMPRINT",EDGE,{"derivedFrom":sQuery(id+"F29.wireOp",EDGE,"E90")}),1.0]])]});
            var Q1;
            Q1=makeQuery(id+"F24.opExtrude","SWEPT_FACE",FACE,{"disambiguationData":[OSD([sQuery(id+"F0.wireOp",EDGE,"E17")])]});
            extrude(context, id + "F32", {"entities" : qUnion([Q0]), "operationType" : NewBodyOperationType.REMOVE, "endBound" : BoundingType.UP_TO_SURFACE, "oppositeDirection" : true, "endBoundEntityFace" : qUnion([Q1]), "depth" : 25 * mm});
        }
        {
            var Q0;
            Q0=qCreatedBy(makeId("Front.planeOp"),FACE);
            var sketch = newSketch(context, id + "F33", { "sketchPlane" : qUnion([Q0])});
            skCircle(sketch, "E91.cCircle", {"center": v(-36.64, 24.3) * mm, "radius": 2.85 * mm, "construction": true});
            skLineSegment(sketch, "E91.0", {"start": v(-33.79, 22.65) * mm, "end": v(-36.64, 21) * mm});
            skLineSegment(sketch, "E91.1", {"start": v(-36.64, 21) * mm, "end": v(-39.49, 22.65) * mm});
            skLineSegment(sketch, "E91.2", {"start": v(-39.49, 22.65) * mm, "end": v(-39.49, 25.94) * mm});
            skLineSegment(sketch, "E91.3", {"start": v(-39.49, 25.94) * mm, "end": v(-36.64, 27.59) * mm});
            skLineSegment(sketch, "E91.4", {"start": v(-36.64, 27.59) * mm, "end": v(-33.79, 25.94) * mm});
            skLineSegment(sketch, "E91.5", {"start": v(-33.79, 25.94) * mm, "end": v(-33.79, 22.65) * mm});
            skPoint(sketch, "E91.0.midPoint", {"position": v(-35.21, 21.83) * mm});
            skCircle(sketch, "E92.cCircle", {"center": v(36.64, 24.3) * mm, "radius": 2.85 * mm, "construction": true});
            skLineSegment(sketch, "E92.0", {"start": v(39.49, 22.65) * mm, "end": v(36.64, 21) * mm});
            skLineSegment(sketch, "E92.1", {"start": v(36.64, 21) * mm, "end": v(33.79, 22.65) * mm});
            skLineSegment(sketch, "E92.2", {"start": v(33.79, 22.65) * mm, "end": v(33.79, 25.94) * mm});
            skLineSegment(sketch, "E92.3", {"start": v(33.79, 25.94) * mm, "end": v(36.64, 27.59) * mm});
            skLineSegment(sketch, "E92.4", {"start": v(36.64, 27.59) * mm, "end": v(39.49, 25.94) * mm});
            skLineSegment(sketch, "E92.5", {"start": v(39.49, 25.94) * mm, "end": v(39.49, 22.65) * mm});
            skPoint(sketch, "E92.0.midPoint", {"position": v(38.06, 21.83) * mm});
            skCircle(sketch, "E93.cCircle", {"center": v(-36.64, -22.69) * mm, "radius": 2.85 * mm, "construction": true});
            skLineSegment(sketch, "E93.0", {"start": v(-33.79, -24.33) * mm, "end": v(-36.64, -25.98) * mm});
            skLineSegment(sketch, "E93.1", {"start": v(-36.64, -25.98) * mm, "end": v(-39.49, -24.33) * mm});
            skLineSegment(sketch, "E93.2", {"start": v(-39.49, -24.33) * mm, "end": v(-39.49, -21.04) * mm});
            skLineSegment(sketch, "E93.3", {"start": v(-39.49, -21.04) * mm, "end": v(-36.64, -19.4) * mm});
            skLineSegment(sketch, "E93.4", {"start": v(-36.64, -19.4) * mm, "end": v(-33.79, -21.04) * mm});
            skLineSegment(sketch, "E93.5", {"start": v(-33.79, -21.04) * mm, "end": v(-33.79, -24.33) * mm});
            skPoint(sketch, "E93.0.midPoint", {"position": v(-35.21, -25.16) * mm});
            skCircle(sketch, "E94.cCircle", {"center": v(36.64, -22.69) * mm, "radius": 2.85 * mm, "construction": true});
            skLineSegment(sketch, "E94.0", {"start": v(39.49, -24.33) * mm, "end": v(36.64, -25.98) * mm});
            skLineSegment(sketch, "E94.1", {"start": v(36.64, -25.98) * mm, "end": v(33.79, -24.33) * mm});
            skLineSegment(sketch, "E94.2", {"start": v(33.79, -24.33) * mm, "end": v(33.79, -21.04) * mm});
            skLineSegment(sketch, "E94.3", {"start": v(33.79, -21.04) * mm, "end": v(36.64, -19.4) * mm});
            skLineSegment(sketch, "E94.4", {"start": v(36.64, -19.4) * mm, "end": v(39.49, -21.04) * mm});
            skLineSegment(sketch, "E94.5", {"start": v(39.49, -21.04) * mm, "end": v(39.49, -24.33) * mm});
            skPoint(sketch, "E94.0.midPoint", {"position": v(38.06, -25.16) * mm});
            skSolve(sketch);
        }
        {
            var Q0;
            Q0=makeQuery(id+"F33.imprint","IMPRINT",FACE,{"disambiguationData":[TD([[makeQuery(id+"F33.imprint","IMPRINT",EDGE,{"derivedFrom":sQuery(id+"F33.wireOp",EDGE,"E91.0")}),-1.0]])]});
            var Q1;
            Q1=makeQuery(id+"F33.imprint","IMPRINT",FACE,{"disambiguationData":[TD([[makeQuery(id+"F33.imprint","IMPRINT",EDGE,{"derivedFrom":sQuery(id+"F33.wireOp",EDGE,"E92.0")}),-1.0]])]});
            var Q2;
            Q2=makeQuery(id+"F33.imprint","IMPRINT",FACE,{"disambiguationData":[TD([[makeQuery(id+"F33.imprint","IMPRINT",EDGE,{"derivedFrom":sQuery(id+"F33.wireOp",EDGE,"E94.0")}),-1.0]])]});
            var Q3;
            Q3=makeQuery(id+"F33.imprint","IMPRINT",FACE,{"disambiguationData":[TD([[makeQuery(id+"F33.imprint","IMPRINT",EDGE,{"derivedFrom":sQuery(id+"F33.wireOp",EDGE,"E93.0")}),-1.0]])]});
            var Q4;
            {var subQ0=sQuery(id+"F29.wireOp",EDGE,"E89.MirrorC");var subQ1=sQuery(id+"F29.wireOp",EDGE,"E82.MirrorC");var subQ2=sQuery(id+"F29.wireOp",EDGE,"E78");var subQ3=sQuery(id+"F27.wireOp",EDGE,"E73.MirrorCS");var subQ4=sQuery(id+"F27.wireOp",EDGE,"E70");var subQ5=sQuery(id+"F0.wireOp",EDGE,"E26");var subQ6=sQuery(id+"F29.wireOp",EDGE,"E85");var subQ7=sQuery(id+"F17.wireOp",EDGE,"E65");var subQ8=sQuery(id+"F0.wireOp",EDGE,"E25");var subQ9=sQuery(id+"F0.wireOp",EDGE,"E21");Q4=makeQuery(id+"F31.boolean.opBoolean","SPLIT",FACE,{"disambiguationData":[TD([makeQuery(id+"F21.opShell","OFFSET_FACE",FACE,{"disambiguationData":[OSD([sQuery(id+"F7.wireOp",EDGE,"E37")])]}),makeQuery(id+"F21.opShell","OFFSET_FACE",FACE,{"disambiguationData":[OSD([sQuery(id+"F7.wireOp",EDGE,"E38"),sQuery(id+"F11.wireOp",EDGE,"E55"),sQuery(id+"F11.wireOp",EDGE,"E56"),sQuery(id+"F11.wireOp",EDGE,"E57"),sQuery(id+"F11.wireOp",EDGE,"E58")])]}),makeQuery(id+"F21.opShell","OFFSET_FACE",FACE,{"disambiguationData":[OSD([sQuery(id+"F4.wireOp",EDGE,"E35"),sQuery(id+"F14.wireOp",EDGE,"E59"),sQuery(id+"F14.wireOp",EDGE,"E60"),sQuery(id+"F14.wireOp",EDGE,"E61"),sQuery(id+"F14.wireOp",EDGE,"E62")])]}),makeQuery(id+"F21.opShell","OFFSET_FACE",FACE,{"disambiguationData":[OSD([sQuery(id+"F4.wireOp",EDGE,"E36")])]}),makeQuery(id+"F21.opShell","OFFSET_FACE",FACE,{"disambiguationData":[OSD([subQ7]),TDD([makeQuery(id+"F18.opExtrude","SWEPT_FACE",FACE,{"disambiguationData":[OSD([subQ7])]})])]}),makeQuery(id+"F25.opExtrude","SWEPT_FACE",FACE,{"disambiguationData":[OSD([subQ5])]}),makeQuery(id+"F26.opExtrude","SWEPT_FACE",FACE,{"disambiguationData":[OSD([subQ5])]}),makeQuery(id+"F28.boolean.opBoolean","COPY",FACE,{"derivedFrom":makeQuery(id+"F28.opExtrude","SWEPT_FACE",FACE,{"disambiguationData":[OSD([subQ4])]})}),makeQuery(id+"F28.boolean.opBoolean","COPY",FACE,{"derivedFrom":makeQuery(id+"F28.opExtrude","CAP_FACE",FACE,{"disambiguationData":[OSD([subQ9,subQ8,subQ4,subQ3])],"isStart":true})}),makeQuery(id+"F28.boolean.opBoolean","COPY",FACE,{"derivedFrom":makeQuery(id+"F28.opExtrude","CAP_FACE",FACE,{"disambiguationData":[OSD([subQ9,subQ8,subQ4,subQ3])],"isStart":false})}),makeQuery(id+"F28.boolean.opBoolean","COPY",FACE,{"derivedFrom":makeQuery(id+"F28.opExtrude","SWEPT_FACE",FACE,{"disambiguationData":[OSD([subQ3])]})}),makeQuery(id+"F30.opFillet","BLEND_FACE",FACE,{"disambiguationData":[OSD([subQ4]),TDD([makeQuery(id+"F28.boolean.opBoolean","COPY",EDGE,{"derivedFrom":makeQuery(id+"F28.opExtrude","CAP_EDGE",EDGE,{"disambiguationData":[OSD([subQ4])],"isStart":true})})])]}),makeQuery(id+"F30.opFillet","BLEND_FACE",FACE,{"disambiguationData":[OSD([subQ4]),TDD([makeQuery(id+"F28.boolean.opBoolean","COPY",EDGE,{"derivedFrom":makeQuery(id+"F28.opExtrude","CAP_EDGE",EDGE,{"disambiguationData":[OSD([subQ4])],"isStart":false})})])]}),makeQuery(id+"F30.opFillet","BLEND_FACE",FACE,{"disambiguationData":[OSD([subQ3]),TDD([makeQuery(id+"F28.boolean.opBoolean","COPY",EDGE,{"derivedFrom":makeQuery(id+"F28.opExtrude","CAP_EDGE",EDGE,{"disambiguationData":[OSD([subQ3])],"isStart":true})})])]}),makeQuery(id+"F30.opFillet","BLEND_FACE",FACE,{"disambiguationData":[OSD([subQ3]),TDD([makeQuery(id+"F28.boolean.opBoolean","COPY",EDGE,{"derivedFrom":makeQuery(id+"F28.opExtrude","CAP_EDGE",EDGE,{"disambiguationData":[OSD([subQ3])],"isStart":false})})])]}),makeQuery(id+"F31.opExtrude","SWEPT_FACE",FACE,{"disambiguationData":[OSD([subQ2])]}),makeQuery(id+"F31.opExtrude","CAP_FACE",FACE,{"disambiguationData":[OSD([subQ2])],"isStart":false}),makeQuery(id+"F31.opExtrude","SWEPT_FACE",FACE,{"disambiguationData":[OSD([subQ1])]}),makeQuery(id+"F31.opExtrude","CAP_FACE",FACE,{"disambiguationData":[OSD([subQ1])],"isStart":false}),makeQuery(id+"F31.opExtrude","SWEPT_FACE",FACE,{"disambiguationData":[OSD([subQ6])]}),makeQuery(id+"F31.opExtrude","CAP_FACE",FACE,{"disambiguationData":[OSD([subQ6])],"isStart":false}),makeQuery(id+"F31.opExtrude","SWEPT_FACE",FACE,{"disambiguationData":[OSD([subQ0])]}),makeQuery(id+"F31.opExtrude","CAP_FACE",FACE,{"disambiguationData":[OSD([subQ0])],"isStart":false})])],"derivedFrom":makeQuery(id+"F26.boolean.opBoolean","MERGE",FACE,{"derivedFrom":[makeQuery(id+"F25.opExtrude","SWEPT_FACE",FACE,{"disambiguationData":[OSD([subQ8])]}),makeQuery(id+"F26.opExtrude","SWEPT_FACE",FACE,{"disambiguationData":[OSD([subQ8])]})]})});}
            extrude(context, id + "F34", {"entities" : qUnion([Q0, Q1, Q2, Q3]), "operationType" : NewBodyOperationType.REMOVE, "endBound" : BoundingType.UP_TO_SURFACE, "oppositeDirection" : true, "endBoundEntityFace" : qUnion([Q4]), "depth" : 25 * mm});
        }
        {
            var Q0;
            Q0=qCreatedBy(makeId("Front.planeOp"),FACE);
            var sketch = newSketch(context, id + "F35", { "sketchPlane" : qUnion([Q0])});
            skCircle(sketch, "E95", {"center": v(-36.64, 24.3) * mm, "radius": 3.25 * mm});
            skCircle(sketch, "E96.MirrorC", {"center": v(36.64, 24.3) * mm, "radius": 3.25 * mm});
            skCircle(sketch, "E97", {"center": v(-36.64, -22.69) * mm, "radius": 3.25 * mm});
            skCircle(sketch, "E98.MirrorC", {"center": v(36.64, -22.69) * mm, "radius": 3.25 * mm});
            skSolve(sketch);
        }
        {
            var Q0;
            Q0=makeQuery(id+"F35.imprint","IMPRINT",FACE,{"disambiguationData":[TD([[makeQuery(id+"F35.imprint","IMPRINT",EDGE,{"derivedFrom":sQuery(id+"F35.wireOp",EDGE,"E95")}),1.0]])]});
            var Q1;
            Q1=makeQuery(id+"F35.imprint","IMPRINT",FACE,{"disambiguationData":[TD([[makeQuery(id+"F35.imprint","IMPRINT",EDGE,{"derivedFrom":sQuery(id+"F35.wireOp",EDGE,"E96.MirrorC")}),-1.0]])]});
            var Q2;
            Q2=makeQuery(id+"F35.imprint","IMPRINT",FACE,{"disambiguationData":[TD([[makeQuery(id+"F35.imprint","IMPRINT",EDGE,{"derivedFrom":sQuery(id+"F35.wireOp",EDGE,"E98.MirrorC")}),-1.0]])]});
            var Q3;
            Q3=makeQuery(id+"F35.imprint","IMPRINT",FACE,{"disambiguationData":[TD([[makeQuery(id+"F35.imprint","IMPRINT",EDGE,{"derivedFrom":sQuery(id+"F35.wireOp",EDGE,"E97")}),1.0]])]});
            extrude(context, id + "F36", {"entities" : qUnion([Q0, Q1, Q2, Q3]), "operationType" : NewBodyOperationType.REMOVE, "oppositeDirection" : true, "depth" : 17 * mm});
        }
        {
            var Q0;
            {var subQ0=sQuery(id+"F1.wireOp",EDGE,"E28.right");var subQ1=sQuery(id+"F1.wireOp",EDGE,"E28.left");var subQ2=sQuery(id+"F1.wireOp",EDGE,"E28.top");var subQ3=sQuery(id+"F1.wireOp",EDGE,"E28.bottom");Q0=makeQuery(id+"F23.boolean.opBoolean","MERGE",FACE,{"derivedFrom":[makeQuery(id+"F21.opShell","OFFSET_FACE",FACE,{"disambiguationData":[OSD([subQ3,subQ2,subQ1,subQ0]),OD(0.0)]}),makeQuery(id+"F21.opShell","OFFSET_FACE",FACE,{"disambiguationData":[OSD([subQ3,subQ2,subQ1,subQ0]),OD(1.0)]}),makeQuery(id+"F21.opShell","OFFSET_FACE",FACE,{"disambiguationData":[OSD([subQ3,subQ2,subQ1,subQ0]),OD(2.0)]}),makeQuery(id+"F21.opShell","OFFSET_FACE",FACE,{"disambiguationData":[OSD([subQ3,subQ2,subQ1,subQ0]),OD(3.0)]}),makeQuery(id+"F23.opExtrude","CAP_FACE",FACE,{"disambiguationData":[OSD([sQuery(id+"F22.wireOp",EDGE,"E68.bottom"),sQuery(id+"F22.wireOp",EDGE,"E68.top"),sQuery(id+"F22.wireOp",EDGE,"E68.left"),sQuery(id+"F22.wireOp",EDGE,"E68.right")])],"isStart":false})]});}
            var sketch = newSketch(context, id + "F37", { "sketchPlane" : qUnion([Q0])});
            skLineSegment(sketch, "E99", {"start": v(-27.97, 14.5) * mm, "end": v(27.97, 14.5) * mm, "construction": true});
            skLineSegment(sketch, "E100", {"start": v(-27.97, -6.5) * mm, "end": v(27.97, -6.5) * mm, "construction": true});
            skLineSegment(sketch, "E101.bottom", {"start": v(-27.87, 14.45) * mm, "end": v(27.87, 14.45) * mm});
            skLineSegment(sketch, "E101.top", {"start": v(-27.87, -6.4) * mm, "end": v(27.87, -6.4) * mm});
            skLineSegment(sketch, "E101.left", {"start": v(-27.87, 14.45) * mm, "end": v(-27.87, -6.4) * mm});
            skLineSegment(sketch, "E101.right", {"start": v(27.87, 14.45) * mm, "end": v(27.87, -6.4) * mm});
            skSolve(sketch);
        }
        {
            var Q0;
            Q0=makeQuery(id+"F37.imprint","IMPRINT",FACE,{"disambiguationData":[TD([[makeQuery(id+"F37.imprint","IMPRINT",EDGE,{"derivedFrom":sQuery(id+"F37.wireOp",EDGE,"E101.bottom")}),-1.0]])]});
            var Q1;
            Q1=makeQuery(id+"F37.imprint","IMPRINT",FACE,{"disambiguationData":[TD([[makeQuery(id+"F37.imprint","IMPRINT",EDGE,{"derivedFrom":makeQuery(id+"F10.boolean.opBoolean","COPY",EDGE,{"derivedFrom":makeQuery(id+"F10.opExtrude","CAP_EDGE",EDGE,{"disambiguationData":[OSD([sQuery(id+"F9.wireOp",EDGE,"E43.bottom")])],"isStart":false})})}),1.0]])]});
            var Q2;
            Q2=makeQuery(id+"F37.imprint","IMPRINT",FACE,{"disambiguationData":[TD([[makeQuery(id+"F37.imprint","IMPRINT",EDGE,{"derivedFrom":makeQuery(id+"F10.boolean.opBoolean","COPY",EDGE,{"derivedFrom":makeQuery(id+"F10.opExtrude","CAP_EDGE",EDGE,{"disambiguationData":[OSD([sQuery(id+"F9.wireOp",EDGE,"E44.left")])],"isStart":false})})}),-1.0]])]});
            var Q3;
            Q3=makeQuery(id+"F37.imprint","IMPRINT",FACE,{"disambiguationData":[TD([[makeQuery(id+"F37.imprint","IMPRINT",EDGE,{"derivedFrom":makeQuery(id+"F10.boolean.opBoolean","COPY",EDGE,{"derivedFrom":makeQuery(id+"F10.opExtrude","CAP_EDGE",EDGE,{"disambiguationData":[OSD([sQuery(id+"F9.wireOp",EDGE,"E45.MirrorCS")])],"isStart":false})})}),-1.0]])]});
            var Q4;
            {var subQ0=sQuery(id+"F9.wireOp",EDGE,"E45.MirrorCS");var subQ1=sQuery(id+"F9.wireOp",EDGE,"E46.MirrorCS");var subQ2=sQuery(id+"F9.wireOp",EDGE,"E48.MirrorCS");Q4=makeQuery(id+"F23.boolean.opBoolean","SPLIT",FACE,{"disambiguationData":[TD([makeQuery(id+"F21.opShell","OFFSET_FACE",FACE,{"disambiguationData":[OSD([subQ0])]})])],"derivedFrom":makeQuery(id+"F21.opShell","OFFSET_FACE",FACE,{"disambiguationData":[OSD([subQ0,subQ1,sQuery(id+"F9.wireOp",EDGE,"E47.MirrorCS"),subQ2])]})});}
            extrude(context, id + "F38", {"entities" : qUnion([Q0, Q1, Q2, Q3]), "endBound" : BoundingType.UP_TO_SURFACE, "depth" : 25 * mm, "endBoundEntityFace" : qUnion([Q4]), "offsetDistance" : 25 * mm});
        }
        {
            var Q0;
            Q0=makeQuery(id+"F2.opExtrude","CAP_FACE",FACE,{"disambiguationData":[OSD([sQuery(id+"F1.wireOp",EDGE,"E28.bottom"),sQuery(id+"F1.wireOp",EDGE,"E28.top"),sQuery(id+"F1.wireOp",EDGE,"E28.left"),sQuery(id+"F1.wireOp",EDGE,"E28.right")])],"isStart":false});
            var sketch = newSketch(context, id + "F39", { "sketchPlane" : qUnion([Q0])});
            skLineSegment(sketch, "E102.bottom", {"start": v(21.9, -5.9) * mm, "end": v(14.1, -5.9) * mm});
            skLineSegment(sketch, "E102.top", {"start": v(21.9, 13.9) * mm, "end": v(14.1, 13.9) * mm});
            skLineSegment(sketch, "E102.left", {"start": v(21.9, -5.9) * mm, "end": v(21.9, 13.9) * mm});
            skLineSegment(sketch, "E102.right", {"start": v(14.1, -5.9) * mm, "end": v(14.1, 13.9) * mm});
            skLineSegment(sketch, "E103.bottom", {"start": v(3.9, -5.9) * mm, "end": v(-3.9, -5.9) * mm});
            skLineSegment(sketch, "E103.top", {"start": v(3.9, 13.9) * mm, "end": v(-3.9, 13.9) * mm});
            skLineSegment(sketch, "E103.left", {"start": v(3.9, -5.9) * mm, "end": v(3.9, 13.9) * mm});
            skLineSegment(sketch, "E103.right", {"start": v(-3.9, -5.9) * mm, "end": v(-3.9, 13.9) * mm});
            skLineSegment(sketch, "E104.bottom", {"start": v(-14.1, -5.9) * mm, "end": v(-21.9, -5.9) * mm});
            skLineSegment(sketch, "E104.top", {"start": v(-14.1, 13.9) * mm, "end": v(-21.9, 13.9) * mm});
            skLineSegment(sketch, "E104.left", {"start": v(-14.1, -5.9) * mm, "end": v(-14.1, 13.9) * mm});
            skLineSegment(sketch, "E104.right", {"start": v(-21.9, -5.9) * mm, "end": v(-21.9, 13.9) * mm});
            skSolve(sketch);
        }
        {
            var Q0;
            Q0=makeQuery(id+"F39.imprint","IMPRINT",FACE,{"disambiguationData":[TD([[makeQuery(id+"F39.imprint","IMPRINT",EDGE,{"derivedFrom":sQuery(id+"F39.wireOp",EDGE,"E102.bottom")}),-1.0]])]});
            var Q1;
            Q1=makeQuery(id+"F39.imprint","IMPRINT",FACE,{"disambiguationData":[TD([[makeQuery(id+"F39.imprint","IMPRINT",EDGE,{"derivedFrom":sQuery(id+"F39.wireOp",EDGE,"E103.bottom")}),-1.0]])]});
            var Q2;
            Q2=makeQuery(id+"F39.imprint","IMPRINT",FACE,{"disambiguationData":[TD([[makeQuery(id+"F39.imprint","IMPRINT",EDGE,{"derivedFrom":sQuery(id+"F39.wireOp",EDGE,"E104.bottom")}),-1.0]])]});
            var Q3;
            Q3=makeQuery(id+"F38.opExtrude","CAP_FACE",FACE,{"disambiguationData":[OSD([sQuery(id+"F37.wireOp",EDGE,"E101.bottom"),sQuery(id+"F37.wireOp",EDGE,"E101.top"),sQuery(id+"F37.wireOp",EDGE,"E101.left"),sQuery(id+"F37.wireOp",EDGE,"E101.right")])],"isStart":true});
            extrude(context, id + "F40", {"entities" : qUnion([Q0, Q1, Q2]), "operationType" : NewBodyOperationType.ADD, "endBound" : BoundingType.UP_TO_SURFACE, "oppositeDirection" : true, "depth" : 25 * mm, "endBoundEntityFace" : qUnion([Q3]), "offsetDistance" : 25 * mm});
        }
        {
            var Q0;
            Q0=makeQuery(id+"F40.opExtrude","CAP_FACE",FACE,{"disambiguationData":[OSD([sQuery(id+"F39.wireOp",EDGE,"E104.bottom"),sQuery(id+"F39.wireOp",EDGE,"E104.top"),sQuery(id+"F39.wireOp",EDGE,"E104.left"),sQuery(id+"F39.wireOp",EDGE,"E104.right")])],"isStart":true});
            var sketch = newSketch(context, id + "F41", { "sketchPlane" : qUnion([Q0])});
            skLineSegment(sketch, "E105", {"start": v(-21.9, 4) * mm, "end": v(21.92, 4) * mm, "construction": true});
            skCircle(sketch, "E106", {"center": v(18.02, 4) * mm, "radius": 1.5 * mm});
            skCircle(sketch, "E107", {"center": v(-18.11, 4) * mm, "radius": 1.5 * mm});
            skCircle(sketch, "E108", {"center": v(-18.11, 9) * mm, "radius": 1.5 * mm});
            skCircle(sketch, "E109", {"center": v(-18.11, -1) * mm, "radius": 1.5 * mm});
            skCircle(sketch, "E110", {"center": v(0, 6.5) * mm, "radius": 1.5 * mm});
            skCircle(sketch, "E111", {"center": v(0, 1.5) * mm, "radius": 1.5 * mm});
            skSolve(sketch);
        }
        {
            var Q0;
            Q0=makeQuery(id+"F41.imprint","IMPRINT",FACE,{"disambiguationData":[TD([[makeQuery(id+"F41.imprint","IMPRINT",EDGE,{"derivedFrom":sQuery(id+"F41.wireOp",EDGE,"E108")}),1.0]])]});
            var Q1;
            Q1=makeQuery(id+"F41.imprint","IMPRINT",FACE,{"disambiguationData":[TD([[makeQuery(id+"F41.imprint","IMPRINT",EDGE,{"derivedFrom":sQuery(id+"F41.wireOp",EDGE,"E107")}),1.0]])]});
            var Q2;
            Q2=makeQuery(id+"F41.imprint","IMPRINT",FACE,{"disambiguationData":[TD([[makeQuery(id+"F41.imprint","IMPRINT",EDGE,{"derivedFrom":sQuery(id+"F41.wireOp",EDGE,"E109")}),1.0]])]});
            var Q3;
            Q3=makeQuery(id+"F41.imprint","IMPRINT",FACE,{"disambiguationData":[TD([[makeQuery(id+"F41.imprint","IMPRINT",EDGE,{"derivedFrom":sQuery(id+"F41.wireOp",EDGE,"E111")}),1.0]])]});
            var Q4;
            Q4=makeQuery(id+"F41.imprint","IMPRINT",FACE,{"disambiguationData":[TD([[makeQuery(id+"F41.imprint","IMPRINT",EDGE,{"derivedFrom":sQuery(id+"F41.wireOp",EDGE,"E110")}),1.0]])]});
            var Q5;
            Q5=makeQuery(id+"F41.imprint","IMPRINT",FACE,{"disambiguationData":[TD([[makeQuery(id+"F41.imprint","IMPRINT",EDGE,{"derivedFrom":sQuery(id+"F41.wireOp",EDGE,"E106")}),1.0]])]});
            extrude(context, id + "F42", {"entities" : qUnion([Q0, Q1, Q2, Q3, Q4, Q5]), "operationType" : NewBodyOperationType.REMOVE, "oppositeDirection" : true, "depth" : 1 * mm, "offsetDistance" : 25 * mm});
        }
    });
